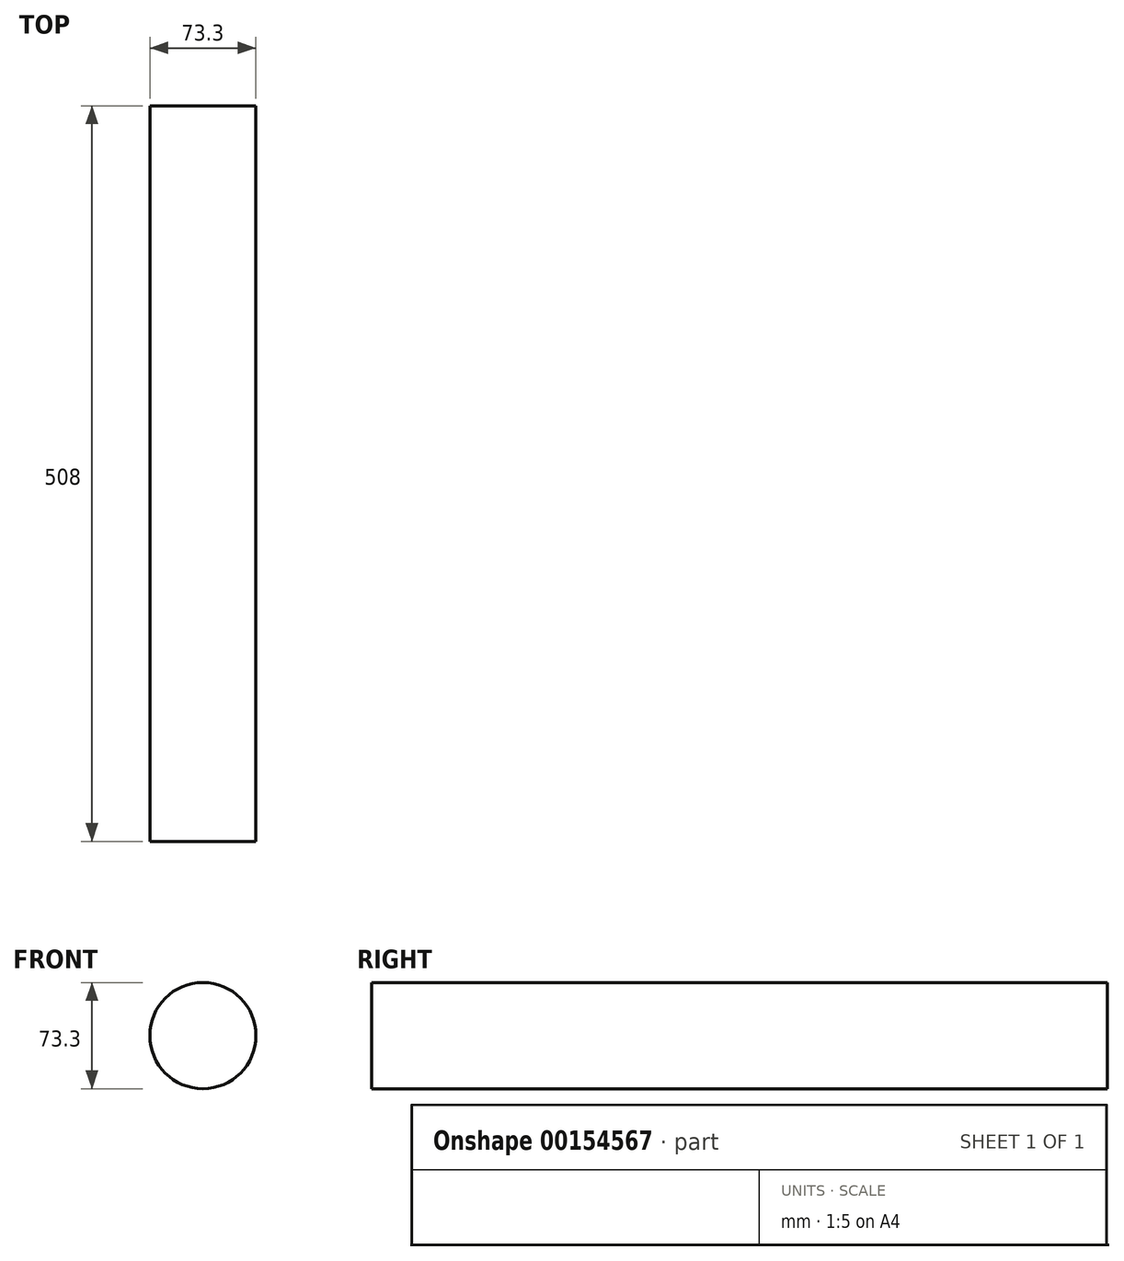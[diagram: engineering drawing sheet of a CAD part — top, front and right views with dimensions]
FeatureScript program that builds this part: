
annotation { "Feature Type Name" : "Feature", "Feature Type Description" : "" }
export const myFeature = defineFeature(function(context is Context, id is Id, definition is map)
    precondition{}
    {
        {
            var Q0;
            Q0=qCreatedBy(makeId("Front.planeOp"),FACE);
            var sketch = newSketch(context, id + "F0", { "sketchPlane" : qUnion([Q0])});
            skCircle(sketch, "E0", {"center": v(0, 0) * mm, "radius": 36.65 * mm});
            skSolve(sketch);
        }
        {
            var Q0;
            Q0=makeQuery(id+"F0.imprint","IMPRINT",FACE,{"disambiguationData":[TD([[makeQuery(id+"F0.imprint","IMPRINT",EDGE,{"derivedFrom":sQuery(id+"F0.wireOp",EDGE,"E0")}),1.0]])]});
            extrude(context, id + "F1", {"entities" : qUnion([Q0]), "endBound" : BoundingType.SYMMETRIC, "depth" : 508 * mm});
        }
    });
